# Revit family: Time Power 160 K singola
name_source: partatom
category: Attrezzatura meccanica
units: mm (PartAtom-declared; Revit-internal decimal feet)

## family parameters
Basato su piano di lavoro = No
Classificazione = Nessuno
Condiviso = Sì
Punto di calcolo locali = No
Quota connettore circolare = Usa diametro
Sempre verticale = Sì
Taglio con vuoti quando caricato = No
Tipo di parte = Normale

## types (1)
- 160 K
    Codice assieme = 301001425
    Date of publishing = 09/06/2020
    Depth = 725 mm  [stored 2.37861 ft]
    Descrizione = Condensing thermal module
    Design country = Italy
    EAN code = 8059616964277
    Edition number = 0
    Efficiency 30% = 109.29%
    Energetic efficiency (92/42/CEE) = n.d.
    Flue outlet = 100 mm  [stored 0.328084 ft]
    Gas Inlet Diameter = 25 mm  [stored 0.082021 ft]
    Height = 837 mm  [stored 2.74606 ft]
    Hydronic Return Diameter = 32 mm  [stored 0.104987 ft]
    Hydronic Supply Diameter = 32 mm  [stored 0.104987 ft]
    IFC Classification = Boiler
    Manufacturer country = Italy
    Manufacturer name = Italtherm S.p.A.
    Material main = Metal
    Material secondary = Plastic
    Max number in cascade = 3
    Maximum heat output 50/30°C = 157.5 kW
    Maximum heat output 80/60°C = 144.6 kW
    Maximum heating heat input = 150.0 kW
    Minimum heat output 50/30°C = 27.0 kW
    Minimum heat output 80/60°C = 23.8 kW
    Modello = Time Power K
    NBS reference Description = Condensing boilers
    Nominal efficiency 50/30°C = 105%
    Nominal efficiency 80/60°C = 96.4%
    Omniclass Description = Condensing boilers
    Power consumption (W) = 480 W
    Power supply | Frequency (Hz) = 50 Hz
    Power supply | Phase = 1
    Power supply | Voltage (V) = 230 V
    Product certification = 0476CQ1281
    Product family = High efficiency condensing systems
    Product group = Boilers for commercial applications
    Produttore = Italtherm
    Prospetto di default = 0 mm  [stored 0 ft]
    Siphon with condensate drain = 25 mm  [stored 0.082021 ft]
    URL = https://www.italtherm.it
    URL ENG = https://en.italtherm.it
    Uniclass 2015 Name = Boilers
    Weight = 105.00 kg
    Width = 600 mm

note: [stored X ft] marks values corroborated as IEEE doubles in the binary element streams (Revit-internal decimal feet)
